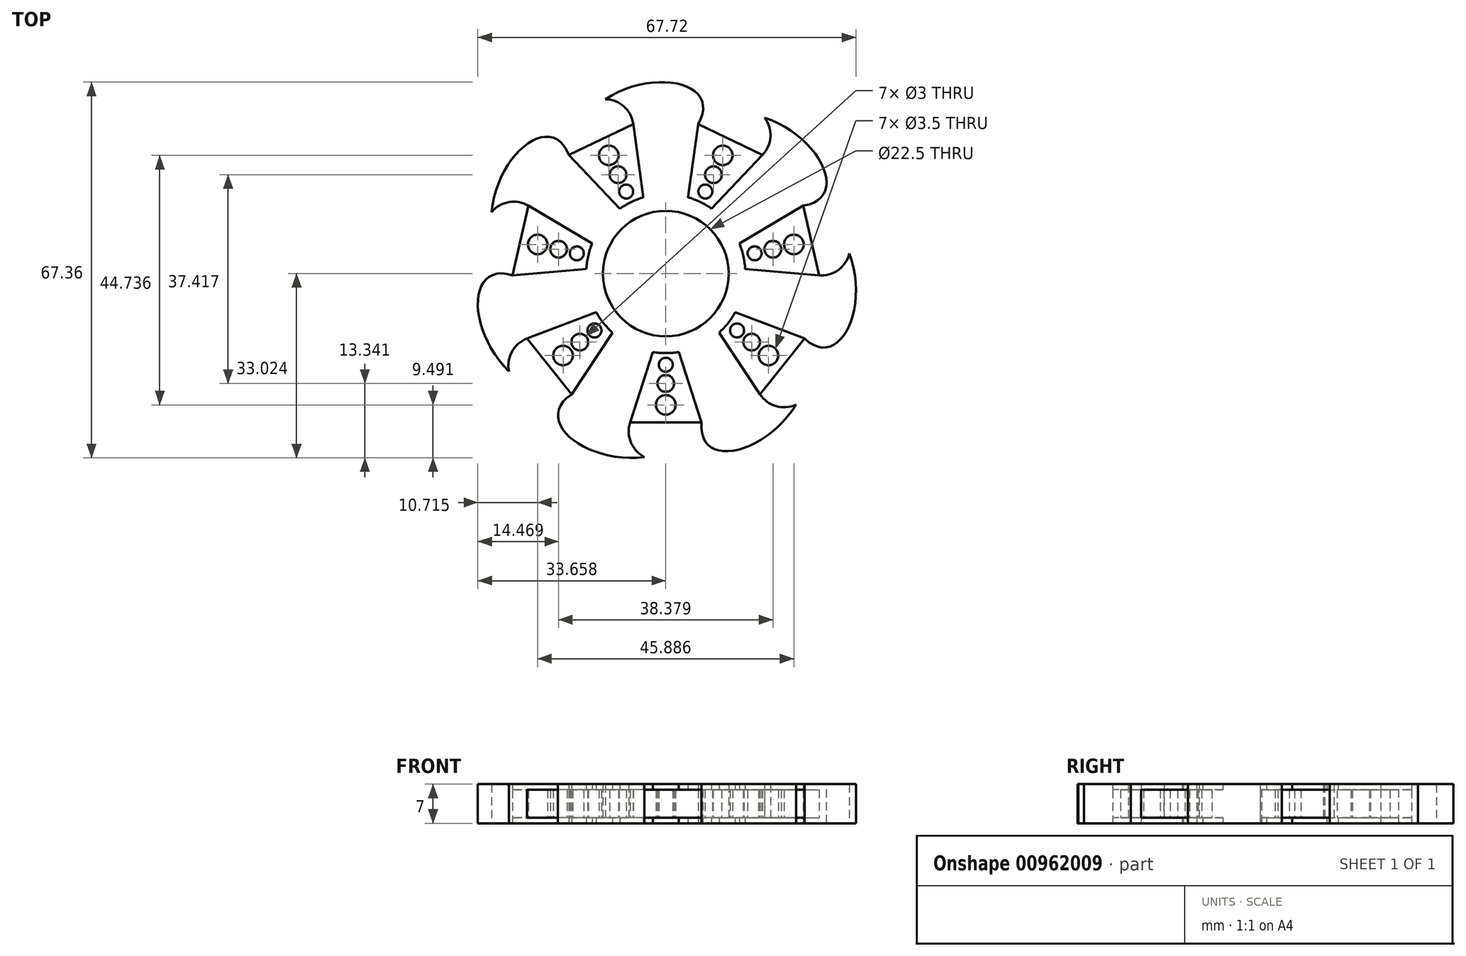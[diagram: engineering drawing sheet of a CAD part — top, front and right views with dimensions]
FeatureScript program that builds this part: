
annotation { "Feature Type Name" : "Feature", "Feature Type Description" : "" }
export const myFeature = defineFeature(function(context is Context, id is Id, definition is map)
    precondition{}
    {
        {
            var Q0;
            Q0=qCreatedBy(makeId("Top.planeOp"),FACE);
            var sketch = newSketch(context, id + "F0", { "sketchPlane" : qUnion([Q0])});
            skCircle(sketch, "E0", {"center": v(-740.96, 663.64) * mm, "radius": 11.25 * mm});
            skCircle(sketch, "E1", {"center": v(-740.96, 663.64) * mm, "radius": 14.25 * mm});
            skLineSegment(sketch, "E2", {"start": v(-740.96, 677.9) * mm, "end": v(-740.96, 685.93) * mm});
            skPoint(sketch, "E3.endSnap0", {"position": v(-736.96, 679.77) * mm});
            skLineSegment(sketch, "E4", {"start": v(-744.96, 677.32) * mm, "end": v(-746.78, 690.47) * mm});
            skLineSegment(sketch, "E5", {"start": v(-736.96, 677.32) * mm, "end": v(-735.14, 690.47) * mm});
            skLineSegment(sketch, "E6.1.0", {"start": v(-749.16, 675.3) * mm, "end": v(-758.3, 684.92) * mm});
            skLineSegment(sketch, "E6.1.1", {"start": v(-754.15, 669.04) * mm, "end": v(-765.56, 675.82) * mm});
            skLineSegment(sketch, "E6.2.0", {"start": v(-755.19, 664.5) * mm, "end": v(-768.4, 663.35) * mm});
            skLineSegment(sketch, "E6.2.1", {"start": v(-753.4, 656.7) * mm, "end": v(-765.82, 652) * mm});
            skLineSegment(sketch, "E6.3.0", {"start": v(-750.5, 653.06) * mm, "end": v(-757.84, 642) * mm});
            skLineSegment(sketch, "E6.3.1", {"start": v(-743.3, 649.59) * mm, "end": v(-747.36, 636.95) * mm});
            skLineSegment(sketch, "E6.4.0", {"start": v(-738.63, 649.59) * mm, "end": v(-734.57, 636.95) * mm});
            skLineSegment(sketch, "E6.4.1", {"start": v(-731.42, 653.06) * mm, "end": v(-724.08, 642) * mm});
            skLineSegment(sketch, "E6.5.0", {"start": v(-728.52, 656.7) * mm, "end": v(-716.1, 652) * mm});
            skLineSegment(sketch, "E6.5.1", {"start": v(-726.74, 664.5) * mm, "end": v(-713.52, 663.35) * mm});
            skLineSegment(sketch, "E6.6.0", {"start": v(-727.77, 669.04) * mm, "end": v(-716.36, 675.82) * mm});
            skLineSegment(sketch, "E6.6.1", {"start": v(-732.76, 675.3) * mm, "end": v(-723.62, 684.92) * mm});
            skArc(sketch, "E7", {"start": v(-746.78, 690.47) * mm, "mid": v(-748.46, 693.61) * mm, "end": v(-751.78, 694.92) * mm});
            skFitSpline(sketch, "E8", {"points": [v(-751.78, 694.92) * mm, v(-735.14, 690.47) * mm], "startDerivative": vector(26.43, 17.21) * mm, "endDerivative": vector(-12.89, -22.13) * mm});
            skArc(sketch, "E9.1.0", {"start": v(-765.56, 675.82) * mm, "mid": v(-769.07, 676.46) * mm, "end": v(-772.16, 674.68) * mm});
            skArc(sketch, "E9.2.0", {"start": v(-765.82, 652) * mm, "mid": v(-768.5, 649.66) * mm, "end": v(-769.04, 646.13) * mm});
            skArc(sketch, "E9.3.0", {"start": v(-747.36, 636.95) * mm, "mid": v(-747.2, 633.39) * mm, "end": v(-744.78, 630.77) * mm});
            skArc(sketch, "E9.4.0", {"start": v(-724.08, 642) * mm, "mid": v(-721.2, 639.9) * mm, "end": v(-717.64, 640.16) * mm});
            skArc(sketch, "E9.5.0", {"start": v(-713.52, 663.35) * mm, "mid": v(-710.08, 664.29) * mm, "end": v(-708.07, 667.24) * mm});
            skArc(sketch, "E9.6.0", {"start": v(-723.62, 684.92) * mm, "mid": v(-722.2, 688.2) * mm, "end": v(-723.26, 691.6) * mm});
            skLineSegment(sketch, "E10.1.0", {"start": v(-768.4, 663.35) * mm, "end": v(-765.56, 675.82) * mm});
            skLineSegment(sketch, "E10.2.0", {"start": v(-757.84, 642) * mm, "end": v(-765.82, 652) * mm});
            skLineSegment(sketch, "E10.3.0", {"start": v(-734.57, 636.95) * mm, "end": v(-747.36, 636.95) * mm});
            skLineSegment(sketch, "E10.4.0", {"start": v(-716.1, 652) * mm, "end": v(-724.08, 642) * mm});
            skLineSegment(sketch, "E10.5.0", {"start": v(-716.36, 675.82) * mm, "end": v(-713.52, 663.35) * mm});
            skLineSegment(sketch, "E10.6.0", {"start": v(-735.14, 690.47) * mm, "end": v(-723.62, 684.92) * mm});
            skLineSegment(sketch, "E11", {"start": v(-749.16, 675.3) * mm, "end": v(-760.89, 687.64) * mm});
            skLineSegment(sketch, "E12", {"start": v(-758.3, 684.92) * mm, "end": v(-746.78, 690.47) * mm});
            skLineSegment(sketch, "E13", {"start": v(-749.16, 675.3) * mm, "end": v(-744.96, 677.32) * mm});
            skLineSegment(sketch, "E14", {"start": v(-747.06, 676.3) * mm, "end": v(-752.54, 687.7) * mm});
            skLineSegment(sketch, "E15", {"start": v(-752.54, 687.7) * mm, "end": v(-749.8, 682) * mm});
            skLineSegment(sketch, "E16", {"start": v(-749.8, 682) * mm, "end": v(-747.06, 676.3) * mm});
            skCircle(sketch, "E17", {"center": v(-751.17, 684.85) * mm, "radius": 1.75 * mm});
            skLineSegment(sketch, "E18", {"start": v(-751.17, 684.85) * mm, "end": v(-748.43, 679.16) * mm});
            skCircle(sketch, "E19", {"center": v(-749.5, 681.38) * mm, "radius": 1.5 * mm});
            skCircle(sketch, "E20", {"center": v(-748.05, 678.36) * mm, "radius": 1.25 * mm});
            skCircle(sketch, "E21.1.0", {"center": v(-763.9, 668.88) * mm, "radius": 1.75 * mm});
            skCircle(sketch, "E21.1.1", {"center": v(-760.15, 668.02) * mm, "radius": 1.5 * mm});
            skCircle(sketch, "E21.1.2", {"center": v(-756.89, 667.28) * mm, "radius": 1.25 * mm});
            skCircle(sketch, "E21.2.0", {"center": v(-759.36, 648.97) * mm, "radius": 1.75 * mm});
            skCircle(sketch, "E21.2.1", {"center": v(-756.35, 651.37) * mm, "radius": 1.5 * mm});
            skCircle(sketch, "E21.2.2", {"center": v(-753.73, 653.46) * mm, "radius": 1.25 * mm});
            skCircle(sketch, "E21.3.0", {"center": v(-740.96, 640.11) * mm, "radius": 1.75 * mm});
            skCircle(sketch, "E21.3.1", {"center": v(-740.96, 643.96) * mm, "radius": 1.5 * mm});
            skCircle(sketch, "E21.3.2", {"center": v(-740.96, 647.31) * mm, "radius": 1.25 * mm});
            skCircle(sketch, "E21.4.0", {"center": v(-722.56, 648.97) * mm, "radius": 1.75 * mm});
            skCircle(sketch, "E21.4.1", {"center": v(-725.57, 651.37) * mm, "radius": 1.5 * mm});
            skCircle(sketch, "E21.4.2", {"center": v(-728.2, 653.46) * mm, "radius": 1.25 * mm});
            skCircle(sketch, "E21.5.0", {"center": v(-718.02, 668.88) * mm, "radius": 1.75 * mm});
            skCircle(sketch, "E21.5.1", {"center": v(-721.77, 668.02) * mm, "radius": 1.5 * mm});
            skCircle(sketch, "E21.5.2", {"center": v(-725.04, 667.28) * mm, "radius": 1.25 * mm});
            skCircle(sketch, "E21.6.0", {"center": v(-730.75, 684.85) * mm, "radius": 1.75 * mm});
            skCircle(sketch, "E21.6.1", {"center": v(-732.42, 681.38) * mm, "radius": 1.5 * mm});
            skCircle(sketch, "E21.6.2", {"center": v(-733.88, 678.36) * mm, "radius": 1.25 * mm});
            skSolve(sketch);
        }
        {
            var Q0;
            {var subQ1=sQuery(id+"F0.wireOp",EDGE,"E4");Q0=makeQuery(id+"F0.imprint","IMPRINT",FACE,{"disambiguationData":[TD([[makeQuery(id+"F0.imprint","IMPRINT",EDGE,{"derivedFrom":subQ1}),-1.0]])]});}
            var Q1;
            Q1=makeQuery(id+"F0.imprint","IMPRINT",FACE,{"disambiguationData":[TD([[makeQuery(id+"F0.imprint","IMPRINT",EDGE,{"derivedFrom":sQuery(id+"F0.wireOp",EDGE,"E0")}),-1.0]])]});
            var Q2;
            Q2=makeQuery(id+"F2.opPattern","COPY",FACE,{"derivedFrom":makeQuery(id+"F1.opExtrude","CAP_FACE",FACE,{"disambiguationData":[OSD([sQuery(id+"F0.wireOp",EDGE,"E0"),sQuery(id+"F0.wireOp",EDGE,"E1"),sQuery(id+"F0.wireOp",EDGE,"E6.1.1"),sQuery(id+"F0.wireOp",EDGE,"E6.2.0"),sQuery(id+"F0.wireOp",EDGE,"E6.2.1"),sQuery(id+"F0.wireOp",EDGE,"E6.3.0"),sQuery(id+"F0.wireOp",EDGE,"E6.3.1"),sQuery(id+"F0.wireOp",EDGE,"E6.4.0"),sQuery(id+"F0.wireOp",EDGE,"E6.4.1"),sQuery(id+"F0.wireOp",EDGE,"E6.5.0"),sQuery(id+"F0.wireOp",EDGE,"E6.5.1"),sQuery(id+"F0.wireOp",EDGE,"E6.6.0"),sQuery(id+"F0.wireOp",EDGE,"E6.6.1"),sQuery(id+"F0.wireOp",EDGE,"E7"),sQuery(id+"F0.wireOp",EDGE,"E8"),sQuery(id+"F0.wireOp",EDGE,"E10.1.0"),sQuery(id+"F0.wireOp",EDGE,"E10.2.0"),sQuery(id+"F0.wireOp",EDGE,"E10.3.0"),sQuery(id+"F0.wireOp",EDGE,"E10.4.0"),sQuery(id+"F0.wireOp",EDGE,"E10.5.0"),sQuery(id+"F0.wireOp",EDGE,"E10.6.0"),sQuery(id+"F0.wireOp",EDGE,"E12"),sQuery(id+"F0.wireOp",EDGE,"E13"),sQuery(id+"F0.wireOp",EDGE,"hItH9A9O-UE1f-AVN2-QdSK-xxtqNPgCFsgT"),sQuery(id+"F0.wireOp",EDGE,"PK0TmmjD-AhNw-vXbI-EZQL-a9q4jjafIxHU"),sQuery(id+"F0.wireOp",EDGE,"0RZY1OqV-8MOl-QpIU-o1jE-b1cXYCi4v4dz"),sQuery(id+"F0.wireOp",EDGE,"WMoKM8go-Ifvn-jbe3-pbQA-8AdgY8jFMewe"),sQuery(id+"F0.wireOp",EDGE,"WaGHFo1D-qrr7-Ky0B-WOFH-e2W5hQMk9CKB"),sQuery(id+"F0.wireOp",EDGE,"GMuQNoxq-V3xk-nH1Y-e02c-8T4hSu34hcST"),sQuery(id+"F0.wireOp",EDGE,"df6fcfb5-7da3-411f-a465-3de40f26db9e.1.0"),sQuery(id+"F0.wireOp",EDGE,"df6fcfb5-7da3-411f-a465-3de40f26db9e.1.1"),sQuery(id+"F0.wireOp",EDGE,"df6fcfb5-7da3-411f-a465-3de40f26db9e.1.2"),sQuery(id+"F0.wireOp",EDGE,"df6fcfb5-7da3-411f-a465-3de40f26db9e.2.0"),sQuery(id+"F0.wireOp",EDGE,"df6fcfb5-7da3-411f-a465-3de40f26db9e.2.1"),sQuery(id+"F0.wireOp",EDGE,"df6fcfb5-7da3-411f-a465-3de40f26db9e.2.2"),sQuery(id+"F0.wireOp",EDGE,"df6fcfb5-7da3-411f-a465-3de40f26db9e.3.0"),sQuery(id+"F0.wireOp",EDGE,"df6fcfb5-7da3-411f-a465-3de40f26db9e.3.1"),sQuery(id+"F0.wireOp",EDGE,"df6fcfb5-7da3-411f-a465-3de40f26db9e.3.2"),sQuery(id+"F0.wireOp",EDGE,"df6fcfb5-7da3-411f-a465-3de40f26db9e.4.0"),sQuery(id+"F0.wireOp",EDGE,"df6fcfb5-7da3-411f-a465-3de40f26db9e.4.1"),sQuery(id+"F0.wireOp",EDGE,"df6fcfb5-7da3-411f-a465-3de40f26db9e.4.2"),sQuery(id+"F0.wireOp",EDGE,"df6fcfb5-7da3-411f-a465-3de40f26db9e.5.0"),sQuery(id+"F0.wireOp",EDGE,"df6fcfb5-7da3-411f-a465-3de40f26db9e.5.1"),sQuery(id+"F0.wireOp",EDGE,"df6fcfb5-7da3-411f-a465-3de40f26db9e.5.2"),sQuery(id+"F0.wireOp",EDGE,"df6fcfb5-7da3-411f-a465-3de40f26db9e.6.0"),sQuery(id+"F0.wireOp",EDGE,"df6fcfb5-7da3-411f-a465-3de40f26db9e.6.1"),sQuery(id+"F0.wireOp",EDGE,"df6fcfb5-7da3-411f-a465-3de40f26db9e.6.2")])],"isStart":false}),"instanceName":"6"});
            extrude(context, id + "F1", {"entities" : qUnion([Q0, Q1, Q2]), "endBound" : BoundingType.SYMMETRIC, "depth" : 7 * mm, "offsetDistance" : 25 * mm});
        }
        {
            var Q0;
            Q0=makeQuery(id+"F1.opExtrude","SWEPT_BODY",BODY,{"disambiguationData":[OSD([sQuery(id+"F0.wireOp",EDGE,"E0"),sQuery(id+"F0.wireOp",EDGE,"E1"),sQuery(id+"F0.wireOp",EDGE,"E4"),sQuery(id+"F0.wireOp",EDGE,"E5"),sQuery(id+"F0.wireOp",EDGE,"E7"),sQuery(id+"F0.wireOp",EDGE,"E8")])]});
            var Q1;
            Q1=makeQuery(id+"F1.opExtrude","CAP_EDGE",EDGE,{"disambiguationData":[OSD([sQuery(id+"F0.wireOp",EDGE,"E0")])],"isStart":false});
            circularPattern(context, id + "F2", {"entities" : qUnion([Q0]), "axis" : qUnion([Q1]), "angle" : 360 * degree, "instanceCount" : 7, "equalSpace" : true});
        }
        {
            var Q0;
            Q0 = qSketchRegion(id + "F0", true);
            extrude(context, id + "F3", {"entities" : qUnion([Q0]), "operationType" : NewBodyOperationType.ADD, "endBound" : BoundingType.SYMMETRIC, "depth" : 5 * mm, "offsetDistance" : 25 * mm});
        }
    });
